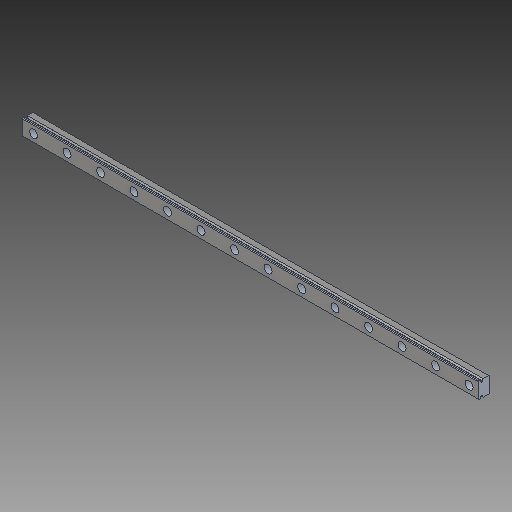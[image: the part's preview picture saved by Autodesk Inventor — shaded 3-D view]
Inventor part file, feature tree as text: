
AUTODESK INVENTOR PART (.ipt)
format: ipt  version: 2019 (Build 230136000, 136)  size: 208,896 bytes
history: native  units: mm
features: extrude x2, sketch x2, fillet x1
ambient origin geometry x8: Origin, YZ Plane, XZ Plane, XY Plane, X Axis, Y Axis, Z Axis, Center Point
bodies: Solid1 (feature_tree)
feature tree (5):
  extrude  "Extrusion3"  Depth=12.0mm
  extrude  "Extrusion4"  Depth=12.0mm
  sketch  "Sketch1"  dims[d0=12.0mm d1=9.0mm]
  fillet  "Fillet1"  Radius=30.0mm
  sketch  "Sketch3"  dims[d8=30.0mm d9=0.0mm d10=12.0mm d11=9.0mm d12=30.0mm d13=0.0mm]
